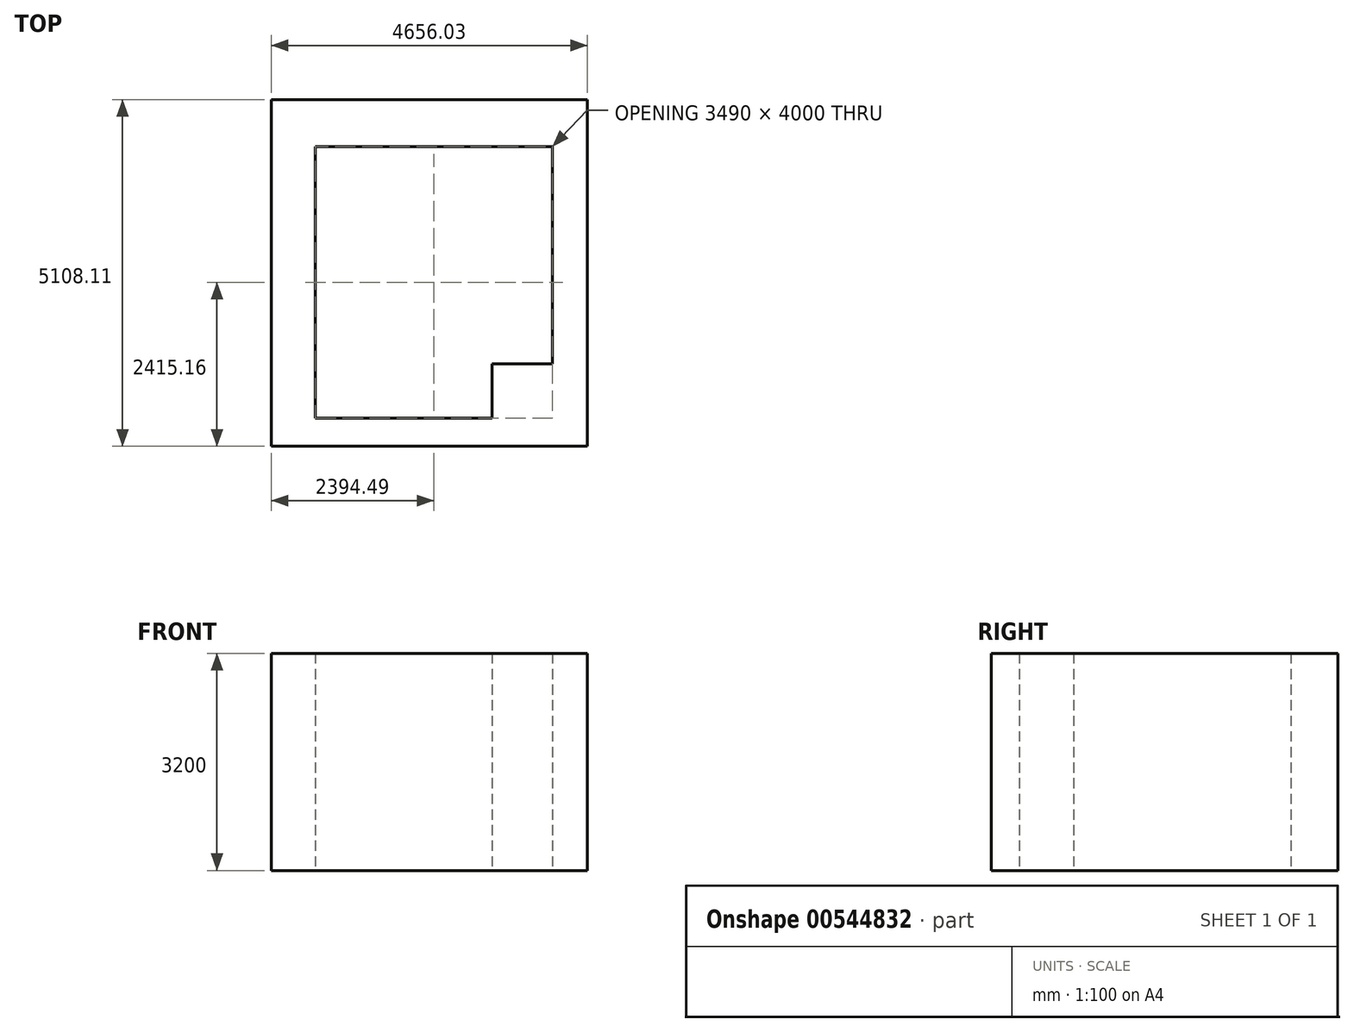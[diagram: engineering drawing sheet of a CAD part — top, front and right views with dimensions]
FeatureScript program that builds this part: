
annotation { "Feature Type Name" : "Feature", "Feature Type Description" : "" }
export const myFeature = defineFeature(function(context is Context, id is Id, definition is map)
    precondition{}
    {
        {
            var Q0;
            Q0=qCreatedBy(makeId("Top.planeOp"),FACE);
            var sketch = newSketch(context, id + "F0", { "sketchPlane" : qUnion([Q0])});
            skLineSegment(sketch, "E0", {"start": v(0, 0) * mm, "end": v(0, 800) * mm});
            skLineSegment(sketch, "E1", {"start": v(0, 800) * mm, "end": v(890, 800) * mm});
            skLineSegment(sketch, "E2", {"start": v(890, 800) * mm, "end": v(890, 4000) * mm});
            skLineSegment(sketch, "E3", {"start": v(890, 4000) * mm, "end": v(-2600, 4000) * mm});
            skLineSegment(sketch, "E4", {"start": v(-2600, 4000) * mm, "end": v(-2600, 0) * mm});
            skLineSegment(sketch, "E5", {"start": v(-2600, 0) * mm, "end": v(0, 0) * mm});
            skLineSegment(sketch, "E6.0", {"start": v(0.25, -0.25) * mm, "end": v(0.25, 800) * mm});
            skLineSegment(sketch, "E6.1", {"start": v(-2600.25, -0.25) * mm, "end": v(0.25, -0.25) * mm});
            skLineSegment(sketch, "E6.2", {"start": v(-2600.25, 4000.25) * mm, "end": v(-2600.25, -0.25) * mm});
            skLineSegment(sketch, "E6.3", {"start": v(890, 4000.25) * mm, "end": v(-2600.25, 4000.25) * mm});
            skLineSegment(sketch, "E7.bottom", {"start": v(-3249.5, 4692.95) * mm, "end": v(1406.54, 4692.95) * mm});
            skLineSegment(sketch, "E7.top", {"start": v(-3249.5, -415.16) * mm, "end": v(1406.54, -415.16) * mm});
            skLineSegment(sketch, "E7.left", {"start": v(-3249.5, 4692.95) * mm, "end": v(-3249.5, -415.16) * mm});
            skLineSegment(sketch, "E7.right", {"start": v(1406.54, 4692.95) * mm, "end": v(1406.54, -415.16) * mm});
            skSolve(sketch);
        }
        {
            var Q0;
            Q0 = qSketchRegion(id + "F0", true);
            extrude(context, id + "F1", {"entities" : qUnion([Q0]), "depth" : 3200 * mm, "offsetDistance" : 25 * mm});
        }
    });
